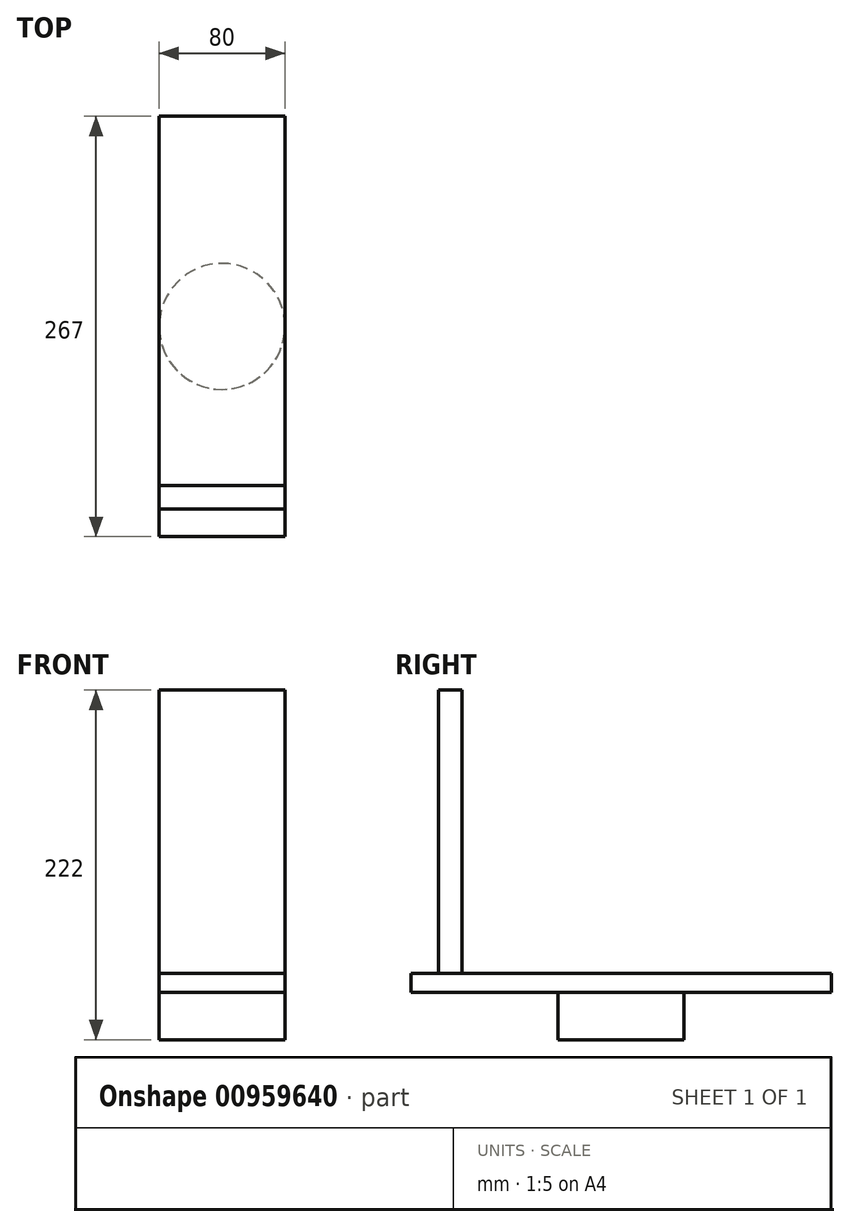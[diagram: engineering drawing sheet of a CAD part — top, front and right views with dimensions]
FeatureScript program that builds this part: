
annotation { "Feature Type Name" : "Feature", "Feature Type Description" : "" }
export const myFeature = defineFeature(function(context is Context, id is Id, definition is map)
    precondition{}
    {
        {
            var Q0;
            Q0=qCreatedBy(makeId("Top.planeOp"),FACE);
            var sketch = newSketch(context, id + "F0", { "sketchPlane" : qUnion([Q0])});
            skCircle(sketch, "E0", {"center": v(0, 0) * mm, "radius": 40 * mm});
            skSolve(sketch);
        }
        {
            var Q0;
            Q0=makeQuery(id+"F0.imprint","IMPRINT",FACE,{"disambiguationData":[TD([[makeQuery(id+"F0.imprint","IMPRINT",EDGE,{"derivedFrom":sQuery(id+"F0.wireOp",EDGE,"E0")}),1.0]])]});
            extrude(context, id + "F1", {"entities" : qUnion([Q0]), "depth" : 30 * mm, "offsetDistance" : 25 * mm});
        }
        {
            var Q0;
            Q0=makeQuery(id+"F1.opExtrude","CAP_FACE",FACE,{"disambiguationData":[OSD([sQuery(id+"F0.wireOp",EDGE,"E0")])],"isStart":false});
            var sketch = newSketch(context, id + "F2", { "sketchPlane" : qUnion([Q0])});
            skLineSegment(sketch, "E1.bottom", {"start": v(40, 133.5) * mm, "end": v(-40, 133.5) * mm});
            skLineSegment(sketch, "E1.top", {"start": v(40, -133.5) * mm, "end": v(-40, -133.5) * mm});
            skLineSegment(sketch, "E1.left", {"start": v(40, 133.5) * mm, "end": v(40, -133.5) * mm});
            skLineSegment(sketch, "E1.right", {"start": v(-40, 133.5) * mm, "end": v(-40, -133.5) * mm});
            skPoint(sketch, "E1.middle", {"position": v(0, 0) * mm});
            skSolve(sketch);
        }
        {
            var Q0;
            {var subQ0=sQuery(id+"F2.wireOp",EDGE,"E1.bottom");Q0=makeQuery(id+"F2.imprint","IMPRINT",FACE,{"disambiguationData":[TD([[makeQuery(id+"F2.imprint","IMPRINT",EDGE,{"derivedFrom":subQ0}),1.0]])]});}
            var Q1;
            {var subQ0=sQuery(id+"F2.wireOp",EDGE,"E1.top");Q1=makeQuery(id+"F2.imprint","IMPRINT",FACE,{"disambiguationData":[TD([[makeQuery(id+"F2.imprint","IMPRINT",EDGE,{"derivedFrom":subQ0}),-1.0]])]});}
            var Q2;
            {var subQ0=makeQuery(id+"F1.opExtrude","CAP_EDGE",EDGE,{"disambiguationData":[OSD([sQuery(id+"F0.wireOp",EDGE,"E0")])],"isStart":false});var subQ1=makeQuery(id+"F2.imprint","INTERSECT",VERTEX,{"derivedFrom":[subQ0,sQuery(id+"F2.wireOp",EDGE,"E1.left")]});Q2=makeQuery(id+"F2.imprint","IMPRINT",FACE,{"disambiguationData":[TD([[makeQuery(id+"F2.imprint","IMPRINT",EDGE,{"disambiguationData":[TD([[subQ1,-1.0]])],"derivedFrom":subQ0}),1.0]])]});}
            extrude(context, id + "F3", {"entities" : qUnion([Q0, Q1, Q2]), "operationType" : NewBodyOperationType.ADD, "depth" : 12 * mm, "offsetDistance" : 25 * mm});
        }
        {
            var Q0;
            Q0=makeQuery(id+"F3.opExtrude","CAP_FACE",FACE,{"disambiguationData":[OSD([sQuery(id+"F2.wireOp",EDGE,"E1.bottom"),sQuery(id+"F2.wireOp",EDGE,"E1.top"),sQuery(id+"F2.wireOp",EDGE,"E1.left"),sQuery(id+"F2.wireOp",EDGE,"E1.right")])],"isStart":false});
            var sketch = newSketch(context, id + "F4", { "sketchPlane" : qUnion([Q0])});
            skLineSegment(sketch, "E2.bottom", {"start": v(-40, -101.06) * mm, "end": v(40, -101.06) * mm});
            skLineSegment(sketch, "E2.top", {"start": v(-40, -116.06) * mm, "end": v(40, -116.06) * mm});
            skLineSegment(sketch, "E2.left", {"start": v(-40, -101.06) * mm, "end": v(-40, -116.06) * mm});
            skLineSegment(sketch, "E2.right", {"start": v(40, -101.06) * mm, "end": v(40, -116.06) * mm});
            skSolve(sketch);
        }
        {
            var Q0;
            Q0=makeQuery(id+"F4.imprint","IMPRINT",FACE,{"disambiguationData":[TD([[makeQuery(id+"F4.imprint","IMPRINT",EDGE,{"derivedFrom":sQuery(id+"F4.wireOp",EDGE,"E2.bottom")}),-1.0]])]});
            extrude(context, id + "F5", {"entities" : qUnion([Q0]), "depth" : 180 * mm, "offsetDistance" : 25 * mm});
        }
    });
